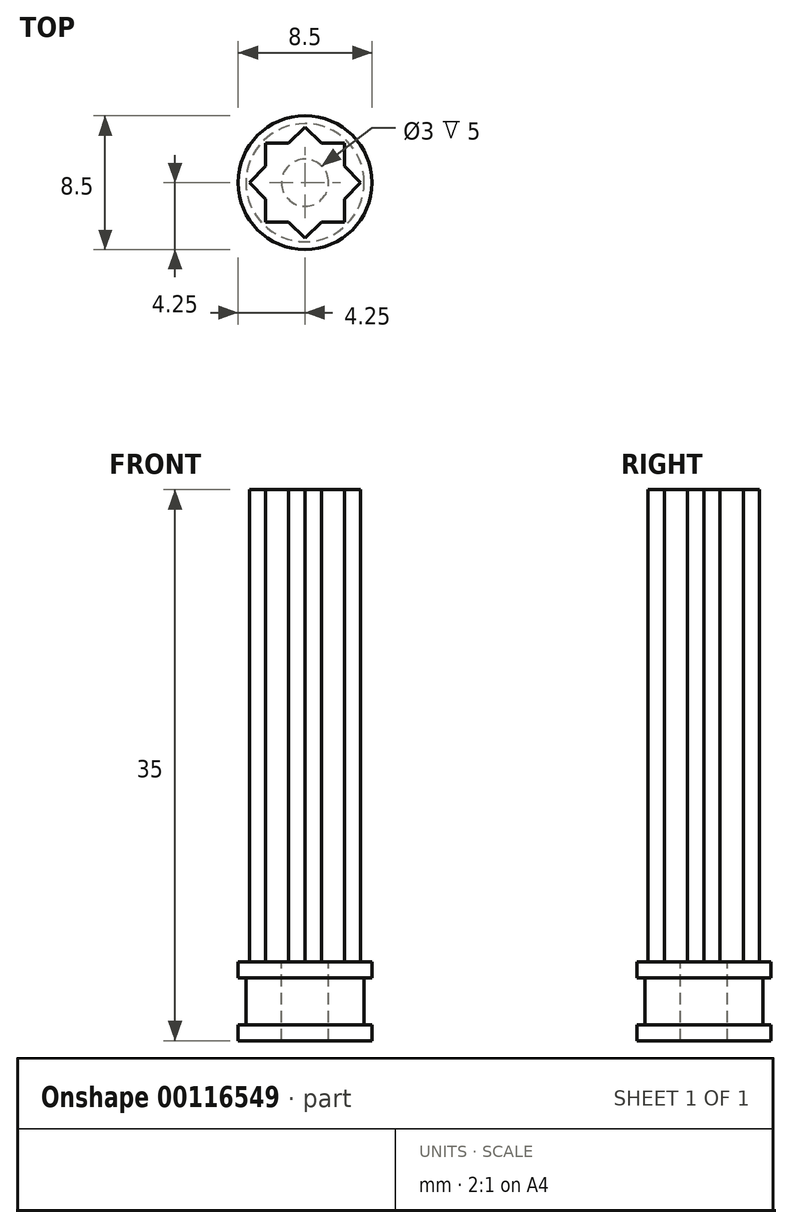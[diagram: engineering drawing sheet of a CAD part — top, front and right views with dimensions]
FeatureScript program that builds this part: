
annotation { "Feature Type Name" : "Feature", "Feature Type Description" : "" }
export const myFeature = defineFeature(function(context is Context, id is Id, definition is map)
    precondition{}
    {
        {
            var Q0;
            Q0=qCreatedBy(makeId("Top.planeOp"),FACE);
            var sketch = newSketch(context, id + "F0", { "sketchPlane" : qUnion([Q0])});
            skLineSegment(sketch, "E0.bottom", {"start": v(-2.5, -2.5) * mm, "end": v(2.5, -2.5) * mm});
            skLineSegment(sketch, "E0.top", {"start": v(-2.5, 2.5) * mm, "end": v(2.5, 2.5) * mm});
            skLineSegment(sketch, "E0.left", {"start": v(-2.5, -2.5) * mm, "end": v(-2.5, 2.5) * mm});
            skLineSegment(sketch, "E0.right", {"start": v(2.5, -2.5) * mm, "end": v(2.5, 2.5) * mm});
            skPoint(sketch, "E0.middle", {"position": v(0, 0) * mm});
            skLineSegment(sketch, "E1", {"start": v(0, 3.54) * mm, "end": v(3.54, 0) * mm});
            skLineSegment(sketch, "E2", {"start": v(3.54, 0) * mm, "end": v(0, -3.54) * mm});
            skLineSegment(sketch, "E3", {"start": v(0, -3.54) * mm, "end": v(-3.54, 0) * mm});
            skLineSegment(sketch, "E4", {"start": v(-3.54, 0) * mm, "end": v(0, 3.54) * mm});
            skSolve(sketch);
        }
        {
            var Q0;
            Q0 = qSketchRegion(id + "F0", true);
            extrude(context, id + "F1", {"entities" : qUnion([Q0]), "depth" : 30 * mm});
        }
        {
            var Q0;
            Q0=makeQuery(id+"F1.opExtrude","CAP_FACE",FACE,{"disambiguationData":[OSD([sQuery(id+"F0.wireOp",EDGE,"E0.bottom"),sQuery(id+"F0.wireOp",EDGE,"E0.top"),sQuery(id+"F0.wireOp",EDGE,"E0.left"),sQuery(id+"F0.wireOp",EDGE,"E0.right"),sQuery(id+"F0.wireOp",EDGE,"E1"),sQuery(id+"F0.wireOp",EDGE,"E2"),sQuery(id+"F0.wireOp",EDGE,"E3"),sQuery(id+"F0.wireOp",EDGE,"E4")])],"isStart":true});
            var sketch = newSketch(context, id + "F2", { "sketchPlane" : qUnion([Q0])});
            skCircle(sketch, "E5", {"center": v(0, 0) * mm, "radius": 4.25 * mm});
            skSolve(sketch);
        }
        {
            var Q0;
            Q0 = qSketchRegion(id + "F2", true);
            extrude(context, id + "F3", {"entities" : qUnion([Q0]), "operationType" : NewBodyOperationType.ADD, "depth" : 5 * mm});
        }
        {
            var Q0;
            Q0=makeQuery(id+"F3.opExtrude","CAP_FACE",FACE,{"disambiguationData":[OSD([sQuery(id+"F2.wireOp",EDGE,"E5")])],"isStart":false});
            cPlane(context, id + "F4", {"entities" : qUnion([Q0]), "cplaneType" : CPlaneType.OFFSET, "offset" : 1 * mm, "oppositeDirection" : true, "width" : 150 * mm, "height" : 150 * mm});
        }
        {
            var Q0;
            Q0=qCreatedBy(id+"F4.planeOp",FACE);
            var sketch = newSketch(context, id + "F5", { "sketchPlane" : qUnion([Q0])});
            skCircle(sketch, "E6", {"center": v(0, 0) * mm, "radius": 4.25 * mm});
            skCircle(sketch, "E7", {"center": v(0, 0) * mm, "radius": 3.75 * mm});
            skSolve(sketch);
        }
        {
            var Q0;
            Q0 = qSketchRegion(id + "F5", true);
            extrude(context, id + "F6", {"entities" : qUnion([Q0]), "operationType" : NewBodyOperationType.REMOVE, "oppositeDirection" : true, "depth" : 3 * mm});
        }
        {
            var Q0;
            Q0=qCreatedBy(makeId("Top.planeOp"),FACE);
            var sketch = newSketch(context, id + "F7", { "sketchPlane" : qUnion([Q0])});
            skCircle(sketch, "E8", {"center": v(0, 0) * mm, "radius": 1.5 * mm});
            skSolve(sketch);
        }
        {
            var Q0;
            Q0 = qSketchRegion(id + "F7", true);
            extrude(context, id + "F8", {"entities" : qUnion([Q0]), "operationType" : NewBodyOperationType.REMOVE, "oppositeDirection" : true, "depth" : 5 * mm});
        }
    });
